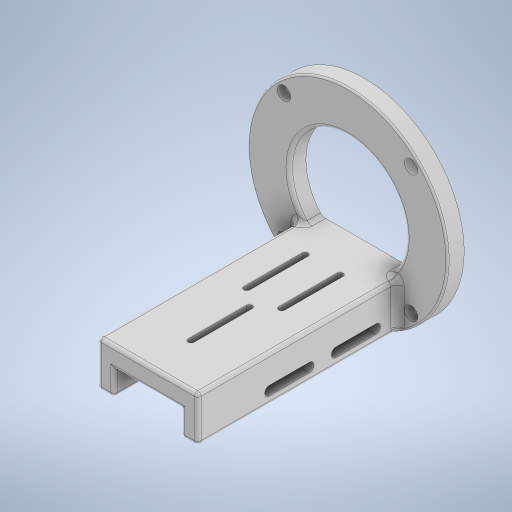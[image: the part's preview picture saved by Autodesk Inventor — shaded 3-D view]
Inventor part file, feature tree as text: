
AUTODESK INVENTOR PART (.ipt)
format: ipt  version: 2023 (Build 270158000, 158)  size: 637,952 bytes
history: native  units: mm
features: sketch x7, extrude x6, fillet x4, hole x2, other x1, pattern_circular x1, projected_geometry x1
ambient origin geometry x8: Origin, YZ Plane, XZ Plane, XY Plane, X Axis, Y Axis, Z Axis, Center Point
bodies: Body1 (feature_tree)
feature tree (22):
  other  "Těleso1"
  extrude  "Vysunutí1"  Depth=120.0mm
  hole  "Díra1"  [1 undecoded]
  pattern_circular  "Kruhové pole1"  [2 undecoded]
  extrude  "Vysunutí2"  TaperAngle=45.0deg  [1 undecoded]
  sketch  "Náčrt5"
  extrude  "Vysunutí4"  Depth=54.0mm
  extrude  "Vysunutí5"  Depth=40.0mm TaperAngle=360.0deg
  fillet  "Zaoblení4"  Radius=60.0mm
  fillet  "Zaoblení5"  Radius=120.0mm
  fillet  "Zaoblení6"  Radius=27.0mm
  fillet  "Zaoblení7"  Radius=12.0mm
  hole  "Díra3"  [1 undecoded]
  extrude  "Vysunutí7"  Depth=3.5mm
  extrude  "Vysunutí8"  Depth=3.5mm
  sketch  "Náčrt1"
  sketch  "Náčrt2"
  sketch  "Náčrt3"
  sketch  "Náčrt9"
  sketch  "Náčrt10"
  sketch  "Náčrt11"
  projected_geometry  "Promítnutá smyčka2"
note: 5 required parameter values undecoded (feature->parameter linkage not recoverable at this tier; creation-order binding heuristic only, values carry confidence <= 0.55)
